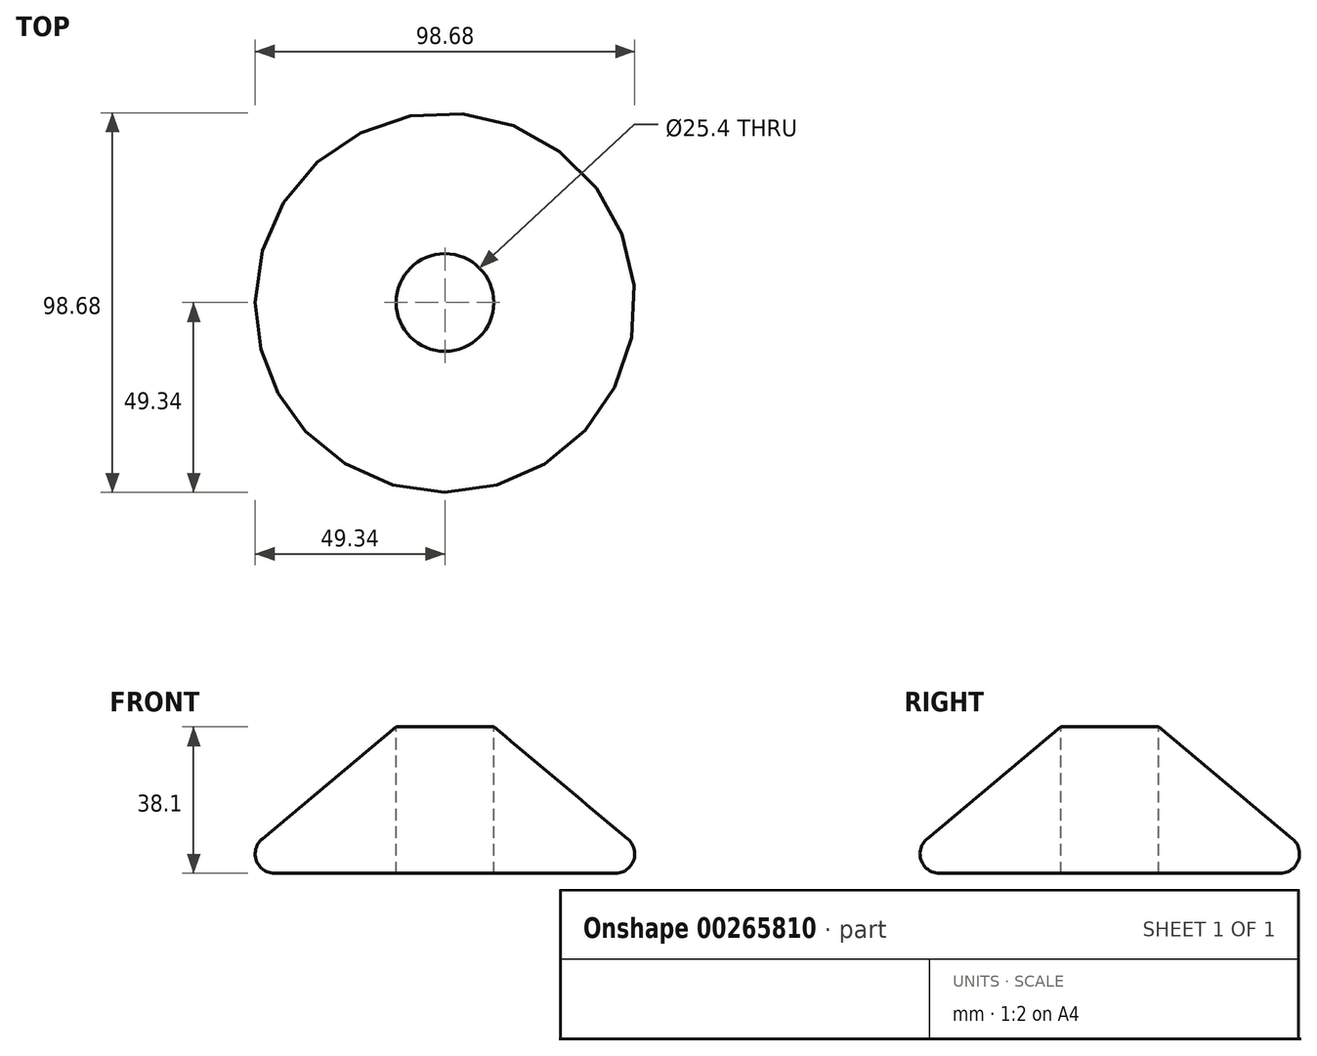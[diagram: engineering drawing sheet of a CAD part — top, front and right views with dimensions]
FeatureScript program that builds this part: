
annotation { "Feature Type Name" : "Feature", "Feature Type Description" : "" }
export const myFeature = defineFeature(function(context is Context, id is Id, definition is map)
    precondition{}
    {
        {
            var Q0;
            Q0=qCreatedBy(makeId("Front.planeOp"),FACE);
            var sketch = newSketch(context, id + "F0", { "sketchPlane" : qUnion([Q0])});
            skLineSegment(sketch, "E0", {"start": v(12.7, 0) * mm, "end": v(12.7, 38.1) * mm});
            skLineSegment(sketch, "E1", {"start": v(12.7, 38.1) * mm, "end": v(58.25, 0) * mm});
            skLineSegment(sketch, "E2", {"start": v(58.25, 0) * mm, "end": v(12.7, 0) * mm});
            skLineSegment(sketch, "E3", {"start": v(12.7, 0) * mm, "end": v(0, 0) * mm});
            skLineSegment(sketch, "E4", {"start": v(0, 48.94) * mm, "end": v(0, 0) * mm});
            skSolve(sketch);
        }
        {
            var Q0;
            Q0=makeQuery(id+"F0.imprint","IMPRINT",FACE,{"disambiguationData":[TD([[makeQuery(id+"F0.imprint","IMPRINT",EDGE,{"derivedFrom":sQuery(id+"F0.wireOp",EDGE,"E0")}),-1.0]])]});
            var Q1;
            Q1=sQuery(id+"F0.wireOp",EDGE,"E4");
            revolve(context, id + "F1", {"entities" : qUnion([Q0]), "axis" : qUnion([Q1]), "revolveType" : RevolveType.FULL});
        }
        {
            var Q0;
            Q0=makeQuery(id+"F1.opRevolve","SWEPT_EDGE",EDGE,{"disambiguationData":[OSD([sQuery(id+"F0.wireOp",EDGE,"E1"),sQuery(id+"F0.wireOp",EDGE,"E2")])]});
            fillet(context, id + "F2", {"entities" : qUnion([Q0]), "radius" : 5.08 * mm, "tangentPropagation" : true, "allowEdgeOverflow" : false});
        }
    });
